annotation { "Feature Type Name" : "Feature", "Feature Type Description" : "" }
export const myFeature = defineFeature(function(context is Context, id is Id, definition is map)
    precondition{}
    {
        {
            var Q0;
            Q0=qCreatedBy(makeId("Front.planeOp"),FACE);
            var sketch = newSketch(context, id + "F0", { "sketchPlane" : qUnion([Q0])});
            skLineSegment(sketch, "E0", {"start": v(0, 0) * mm, "end": v(-59.66, 0) * mm, "construction": true});
            skArc(sketch, "E1", {"start": v(-4.94, 52) * mm, "mid": v(-30.96, 44.87) * mm, "end": v(-49.36, 25.14) * mm});
            skLineSegment(sketch, "E2", {"start": v(-4.94, 52) * mm, "end": v(-4.94, 48.83) * mm});
            skLineSegment(sketch, "E3", {"start": v(-4.94, 48.83) * mm, "end": v(2.13, 48.83) * mm});
            skLineSegment(sketch, "E4", {"start": v(2.13, 48.83) * mm, "end": v(4, 52) * mm});
            skLineSegment(sketch, "E5", {"start": v(4, 52) * mm, "end": v(31.08, 52) * mm});
            skLineSegment(sketch, "E6", {"start": v(31.08, 52) * mm, "end": v(32.87, 50.92) * mm});
            skLineSegment(sketch, "E7", {"start": v(32.87, 50.92) * mm, "end": v(38.57, 40.14) * mm});
            skLineSegment(sketch, "E8", {"start": v(38.57, 40.14) * mm, "end": v(45.19, 36.28) * mm});
            skLineSegment(sketch, "E9", {"start": v(45.19, 36.28) * mm, "end": v(45.19, 32) * mm});
            skLineSegment(sketch, "E10", {"start": v(45.19, 32) * mm, "end": v(39.54, 30.64) * mm});
            skLineSegment(sketch, "E11", {"start": v(39.54, 30.64) * mm, "end": v(37.92, 28.14) * mm});
            skLineSegment(sketch, "E12", {"start": v(37.92, 28.14) * mm, "end": v(2.13, 28.14) * mm});
            skLineSegment(sketch, "E13", {"start": v(2.13, 28.14) * mm, "end": v(2.13, 23.6) * mm});
            skLineSegment(sketch, "E14", {"start": v(2.13, 23.6) * mm, "end": v(17.62, 9.9) * mm});
            skLineSegment(sketch, "E15", {"start": v(17.62, 9.9) * mm, "end": v(45.2, 9.9) * mm});
            skLineSegment(sketch, "E16", {"start": v(45.2, 9.9) * mm, "end": v(45.2, 6.04) * mm});
            skLineSegment(sketch, "E17", {"start": v(45.2, 6.04) * mm, "end": v(57.9, 6.04) * mm});
            skLineSegment(sketch, "E18", {"start": v(57.9, 6.04) * mm, "end": v(59.26, 4.95) * mm});
            skLineSegment(sketch, "E19", {"start": v(59.26, 4.95) * mm, "end": v(59.26, 0) * mm});
            skLineSegment(sketch, "E20", {"start": v(-49.36, 25.14) * mm, "end": v(-53.32, 25.14) * mm});
            skLineSegment(sketch, "E21", {"start": v(-53.32, 25.14) * mm, "end": v(-53.32, 22.85) * mm});
            skLineSegment(sketch, "E22", {"start": v(-53.32, 22.85) * mm, "end": v(-56.28, 21.25) * mm});
            skLineSegment(sketch, "E23", {"start": v(-56.28, 21.25) * mm, "end": v(-56.28, 14.94) * mm});
            skLineSegment(sketch, "E24", {"start": v(-56.28, 14.94) * mm, "end": v(-57.5, 13.21) * mm});
            skLineSegment(sketch, "E25", {"start": v(-57.5, 13.21) * mm, "end": v(-58.56, 3.76) * mm});
            skLineSegment(sketch, "E26", {"start": v(-58.56, 3.76) * mm, "end": v(-58.56, 0) * mm});
            skLineSegment(sketch, "E27.MirrorCS", {"start": v(-56.28, -14.94) * mm, "end": v(-57.5, -13.21) * mm});
            skLineSegment(sketch, "E28.MirrorCS", {"start": v(-57.5, -13.21) * mm, "end": v(-58.56, -3.76) * mm});
            skLineSegment(sketch, "E29.MirrorCS", {"start": v(-58.56, -3.76) * mm, "end": v(-58.56, 0) * mm});
            skLineSegment(sketch, "E30.MirrorCS", {"start": v(-56.28, -21.25) * mm, "end": v(-56.28, -14.94) * mm});
            skLineSegment(sketch, "E31.MirrorCS", {"start": v(-53.32, -22.85) * mm, "end": v(-56.28, -21.25) * mm});
            skLineSegment(sketch, "E32.MirrorCS", {"start": v(-53.32, -25.14) * mm, "end": v(-53.32, -22.85) * mm});
            skLineSegment(sketch, "E33.MirrorCS", {"start": v(-49.36, -25.14) * mm, "end": v(-53.32, -25.14) * mm});
            skArc(sketch, "E34.MirrorCS", {"start": v(-4.94, -52) * mm, "mid": v(-30.96, -44.87) * mm, "end": v(-49.36, -25.14) * mm});
            skLineSegment(sketch, "E35.MirrorCS", {"start": v(-4.94, -52) * mm, "end": v(-4.94, -48.83) * mm});
            skLineSegment(sketch, "E36.MirrorCS", {"start": v(-4.94, -48.83) * mm, "end": v(2.13, -48.83) * mm});
            skLineSegment(sketch, "E37.MirrorCS", {"start": v(2.13, -48.83) * mm, "end": v(4, -52) * mm});
            skLineSegment(sketch, "E38.MirrorCS", {"start": v(4, -52) * mm, "end": v(31.08, -52) * mm});
            skLineSegment(sketch, "E39.MirrorCS", {"start": v(31.08, -52) * mm, "end": v(32.87, -50.92) * mm});
            skLineSegment(sketch, "E40.MirrorCS", {"start": v(38.57, -40.14) * mm, "end": v(45.19, -36.28) * mm});
            skLineSegment(sketch, "E41.MirrorCS", {"start": v(32.87, -50.92) * mm, "end": v(38.57, -40.14) * mm});
            skLineSegment(sketch, "E42", {"start": v(45.19, -36.28) * mm, "end": v(45.19, -31.9) * mm});
            skLineSegment(sketch, "E43", {"start": v(45.19, -31.9) * mm, "end": v(39.54, -30.54) * mm});
            skLineSegment(sketch, "E44", {"start": v(39.54, -30.54) * mm, "end": v(37.55, -27.38) * mm});
            skLineSegment(sketch, "E45", {"start": v(37.55, -27.38) * mm, "end": v(37.55, -12.3) * mm});
            skLineSegment(sketch, "E46", {"start": v(37.55, -12.3) * mm, "end": v(39.67, -9.9) * mm});
            skLineSegment(sketch, "E47", {"start": v(39.67, -9.9) * mm, "end": v(45.19, -9.9) * mm});
            skLineSegment(sketch, "E48", {"start": v(45.19, -9.9) * mm, "end": v(45.2, -6) * mm});
            skLineSegment(sketch, "E49", {"start": v(45.2, -6) * mm, "end": v(57.9, -6.04) * mm});
            skLineSegment(sketch, "E50", {"start": v(57.9, -6.04) * mm, "end": v(59.26, -4.79) * mm});
            skLineSegment(sketch, "E51", {"start": v(59.26, -4.79) * mm, "end": v(59.26, 0) * mm});
            skSolve(sketch);
        }
        {
            var Q0;
            Q0 = qSketchRegion(id + "F0", true);
            extrude(context, id + "F1", {"entities" : qUnion([Q0]), "depth" : 2 * mm, "offsetDistance" : 25 * mm});
        }
        {
            var Q0;
            Q0=makeQuery(id+"F1.opExtrude","SWEPT_BODY",BODY,{"disambiguationData":[OSD([sQuery(id+"F0.wireOp",EDGE,"E1"),sQuery(id+"F0.wireOp",EDGE,"E2"),sQuery(id+"F0.wireOp",EDGE,"E3"),sQuery(id+"F0.wireOp",EDGE,"E4"),sQuery(id+"F0.wireOp",EDGE,"E5"),sQuery(id+"F0.wireOp",EDGE,"E6"),sQuery(id+"F0.wireOp",EDGE,"E7"),sQuery(id+"F0.wireOp",EDGE,"E8"),sQuery(id+"F0.wireOp",EDGE,"E9"),sQuery(id+"F0.wireOp",EDGE,"E10"),sQuery(id+"F0.wireOp",EDGE,"E11"),sQuery(id+"F0.wireOp",EDGE,"E12"),sQuery(id+"F0.wireOp",EDGE,"E13"),sQuery(id+"F0.wireOp",EDGE,"E14"),sQuery(id+"F0.wireOp",EDGE,"E15"),sQuery(id+"F0.wireOp",EDGE,"E16"),sQuery(id+"F0.wireOp",EDGE,"E17"),sQuery(id+"F0.wireOp",EDGE,"E18"),sQuery(id+"F0.wireOp",EDGE,"E19"),sQuery(id+"F0.wireOp",EDGE,"E20"),sQuery(id+"F0.wireOp",EDGE,"E21"),sQuery(id+"F0.wireOp",EDGE,"E22"),sQuery(id+"F0.wireOp",EDGE,"E23"),sQuery(id+"F0.wireOp",EDGE,"E24"),sQuery(id+"F0.wireOp",EDGE,"E25"),sQuery(id+"F0.wireOp",EDGE,"E26"),sQuery(id+"F0.wireOp",EDGE,"E27.MirrorCS"),sQuery(id+"F0.wireOp",EDGE,"E28.MirrorCS"),sQuery(id+"F0.wireOp",EDGE,"E29.MirrorCS"),sQuery(id+"F0.wireOp",EDGE,"E30.MirrorCS"),sQuery(id+"F0.wireOp",EDGE,"E31.MirrorCS"),sQuery(id+"F0.wireOp",EDGE,"E32.MirrorCS"),sQuery(id+"F0.wireOp",EDGE,"E33.MirrorCS"),sQuery(id+"F0.wireOp",EDGE,"E34.MirrorCS"),sQuery(id+"F0.wireOp",EDGE,"E35.MirrorCS"),sQuery(id+"F0.wireOp",EDGE,"E36.MirrorCS"),sQuery(id+"F0.wireOp",EDGE,"E37.MirrorCS"),sQuery(id+"F0.wireOp",EDGE,"E38.MirrorCS"),sQuery(id+"F0.wireOp",EDGE,"E39.MirrorCS"),sQuery(id+"F0.wireOp",EDGE,"E40.MirrorCS"),sQuery(id+"F0.wireOp",EDGE,"E41.MirrorCS"),sQuery(id+"F0.wireOp",EDGE,"E42"),sQuery(id+"F0.wireOp",EDGE,"E43"),sQuery(id+"F0.wireOp",EDGE,"E44"),sQuery(id+"F0.wireOp",EDGE,"E45"),sQuery(id+"F0.wireOp",EDGE,"E46"),sQuery(id+"F0.wireOp",EDGE,"E47"),sQuery(id+"F0.wireOp",EDGE,"E48"),sQuery(id+"F0.wireOp",EDGE,"E49"),sQuery(id+"F0.wireOp",EDGE,"E50"),sQuery(id+"F0.wireOp",EDGE,"E51")])]});
            var Q1;
            Q1=makeQuery(id+"F1.opExtrude","CAP_VERTEX",VERTEX,{"disambiguationData":[OSD([sQuery(id+"F0.wireOp",EDGE,"E19"),sQuery(id+"F0.wireOp",EDGE,"E51")])],"isStart":false});
            transform(context, id + "F2", {"entities" : qUnion([Q0]), "transformType" : TransformType.SCALE_UNIFORMLY, "scale" : 1.25, "scalePoint" : qUnion([Q1]), "makeCopy" : false});
        }
        {
            var Q0;
            Q0=makeQuery(id+"F1.opExtrude","CAP_FACE",FACE,{"disambiguationData":[OSD([sQuery(id+"F0.wireOp",EDGE,"E1"),sQuery(id+"F0.wireOp",EDGE,"E2"),sQuery(id+"F0.wireOp",EDGE,"E3"),sQuery(id+"F0.wireOp",EDGE,"E4"),sQuery(id+"F0.wireOp",EDGE,"E5"),sQuery(id+"F0.wireOp",EDGE,"E6"),sQuery(id+"F0.wireOp",EDGE,"E7"),sQuery(id+"F0.wireOp",EDGE,"E8"),sQuery(id+"F0.wireOp",EDGE,"E9"),sQuery(id+"F0.wireOp",EDGE,"E10"),sQuery(id+"F0.wireOp",EDGE,"E11"),sQuery(id+"F0.wireOp",EDGE,"E12"),sQuery(id+"F0.wireOp",EDGE,"E13"),sQuery(id+"F0.wireOp",EDGE,"E14"),sQuery(id+"F0.wireOp",EDGE,"E15"),sQuery(id+"F0.wireOp",EDGE,"E16"),sQuery(id+"F0.wireOp",EDGE,"E17"),sQuery(id+"F0.wireOp",EDGE,"E18"),sQuery(id+"F0.wireOp",EDGE,"E19"),sQuery(id+"F0.wireOp",EDGE,"E20"),sQuery(id+"F0.wireOp",EDGE,"E21"),sQuery(id+"F0.wireOp",EDGE,"E22"),sQuery(id+"F0.wireOp",EDGE,"E23"),sQuery(id+"F0.wireOp",EDGE,"E24"),sQuery(id+"F0.wireOp",EDGE,"E25"),sQuery(id+"F0.wireOp",EDGE,"E26"),sQuery(id+"F0.wireOp",EDGE,"E27.MirrorCS"),sQuery(id+"F0.wireOp",EDGE,"E28.MirrorCS"),sQuery(id+"F0.wireOp",EDGE,"E29.MirrorCS"),sQuery(id+"F0.wireOp",EDGE,"E30.MirrorCS"),sQuery(id+"F0.wireOp",EDGE,"E31.MirrorCS"),sQuery(id+"F0.wireOp",EDGE,"E32.MirrorCS"),sQuery(id+"F0.wireOp",EDGE,"E33.MirrorCS"),sQuery(id+"F0.wireOp",EDGE,"E34.MirrorCS"),sQuery(id+"F0.wireOp",EDGE,"E35.MirrorCS"),sQuery(id+"F0.wireOp",EDGE,"E36.MirrorCS"),sQuery(id+"F0.wireOp",EDGE,"E37.MirrorCS"),sQuery(id+"F0.wireOp",EDGE,"E38.MirrorCS"),sQuery(id+"F0.wireOp",EDGE,"E39.MirrorCS"),sQuery(id+"F0.wireOp",EDGE,"E40.MirrorCS"),sQuery(id+"F0.wireOp",EDGE,"E41.MirrorCS"),sQuery(id+"F0.wireOp",EDGE,"E42"),sQuery(id+"F0.wireOp",EDGE,"E43"),sQuery(id+"F0.wireOp",EDGE,"E44"),sQuery(id+"F0.wireOp",EDGE,"E45"),sQuery(id+"F0.wireOp",EDGE,"E46"),sQuery(id+"F0.wireOp",EDGE,"E47"),sQuery(id+"F0.wireOp",EDGE,"E48"),sQuery(id+"F0.wireOp",EDGE,"E49"),sQuery(id+"F0.wireOp",EDGE,"E50"),sQuery(id+"F0.wireOp",EDGE,"E51")])],"isStart":false});
            var sketch = newSketch(context, id + "F3", { "sketchPlane" : qUnion([Q0])});
            skLineSegment(sketch, "E52.bottom", {"start": v(-24.37, -61.04) * mm, "end": v(-4.37, -61.04) * mm});
            skLineSegment(sketch, "E52.top", {"start": v(-24.37, -71.04) * mm, "end": v(-4.37, -71.04) * mm});
            skLineSegment(sketch, "E52.left", {"start": v(-24.37, -61.04) * mm, "end": v(-24.37, -71.04) * mm});
            skLineSegment(sketch, "E52.right", {"start": v(-4.37, -61.04) * mm, "end": v(-4.37, -71.04) * mm});
            skLineSegment(sketch, "E53", {"start": v(-88.01, 0) * mm, "end": v(59.26, 0) * mm, "construction": true});
            skLineSegment(sketch, "E54", {"start": v(-14.37, 0) * mm, "end": v(-14.37, -61.04) * mm, "construction": true});
            skLineSegment(sketch, "E55", {"start": v(-24.37, -71.04) * mm, "end": v(-62.79, -71.04) * mm});
            skLineSegment(sketch, "E56", {"start": v(-62.79, -71.04) * mm, "end": v(-72.79, -76.81) * mm});
            skLineSegment(sketch, "E57", {"start": v(-72.79, -76.81) * mm, "end": v(-72.79, -89.04) * mm});
            skLineSegment(sketch, "E58.MirrorCS", {"start": v(-4.37, -71.04) * mm, "end": v(34.04, -71.04) * mm});
            skLineSegment(sketch, "E59.MirrorCS", {"start": v(34.04, -71.04) * mm, "end": v(44.04, -76.81) * mm});
            skLineSegment(sketch, "E60.MirrorCS", {"start": v(44.04, -76.81) * mm, "end": v(44.04, -89.04) * mm});
            skLineSegment(sketch, "E61", {"start": v(-72.79, -89.04) * mm, "end": v(44.04, -89.04) * mm});
            skText(sketch, "E62", { "text": "EBON HAWK", "fontName": "OpenSans-Bold.ttf"});
            skLineSegment(sketch, "E63", {"start": v(-62.79, -89.04) * mm, "end": v(-42.58, -124.04) * mm});
            skLineSegment(sketch, "E64", {"start": v(-42.58, -124.04) * mm, "end": v(13.83, -124.04) * mm});
            skLineSegment(sketch, "E65", {"start": v(13.83, -124.04) * mm, "end": v(34.04, -89.04) * mm});
            skLineSegment(sketch, "E66.0", {"start": v(8.06, -114.04) * mm, "end": v(22.5, -89.04) * mm});
            skLineSegment(sketch, "E66.1", {"start": v(-36.8, -114.04) * mm, "end": v(8.06, -114.04) * mm});
            skLineSegment(sketch, "E66.2", {"start": v(-51.24, -89.04) * mm, "end": v(-36.8, -114.04) * mm});
            const initialGuessF3  = {"E62": [-0.05779, -0.08504, 1, 0, 0.01]};
            skSetInitialGuess(sketch, initialGuessF3);
            skSolve(sketch);
        }
        {
            var Q0;
            Q0 = qSketchRegion(id + "F3", true);
            var Q1;
            Q1=makeQuery(id+"F1.opExtrude","CAP_FACE",FACE,{"disambiguationData":[OSD([sQuery(id+"F0.wireOp",EDGE,"E1"),sQuery(id+"F0.wireOp",EDGE,"E2"),sQuery(id+"F0.wireOp",EDGE,"E3"),sQuery(id+"F0.wireOp",EDGE,"E4"),sQuery(id+"F0.wireOp",EDGE,"E5"),sQuery(id+"F0.wireOp",EDGE,"E6"),sQuery(id+"F0.wireOp",EDGE,"E7"),sQuery(id+"F0.wireOp",EDGE,"E8"),sQuery(id+"F0.wireOp",EDGE,"E9"),sQuery(id+"F0.wireOp",EDGE,"E10"),sQuery(id+"F0.wireOp",EDGE,"E11"),sQuery(id+"F0.wireOp",EDGE,"E12"),sQuery(id+"F0.wireOp",EDGE,"E13"),sQuery(id+"F0.wireOp",EDGE,"E14"),sQuery(id+"F0.wireOp",EDGE,"E15"),sQuery(id+"F0.wireOp",EDGE,"E16"),sQuery(id+"F0.wireOp",EDGE,"E17"),sQuery(id+"F0.wireOp",EDGE,"E18"),sQuery(id+"F0.wireOp",EDGE,"E19"),sQuery(id+"F0.wireOp",EDGE,"E20"),sQuery(id+"F0.wireOp",EDGE,"E21"),sQuery(id+"F0.wireOp",EDGE,"E22"),sQuery(id+"F0.wireOp",EDGE,"E23"),sQuery(id+"F0.wireOp",EDGE,"E24"),sQuery(id+"F0.wireOp",EDGE,"E25"),sQuery(id+"F0.wireOp",EDGE,"E26"),sQuery(id+"F0.wireOp",EDGE,"E27.MirrorCS"),sQuery(id+"F0.wireOp",EDGE,"E28.MirrorCS"),sQuery(id+"F0.wireOp",EDGE,"E29.MirrorCS"),sQuery(id+"F0.wireOp",EDGE,"E30.MirrorCS"),sQuery(id+"F0.wireOp",EDGE,"E31.MirrorCS"),sQuery(id+"F0.wireOp",EDGE,"E32.MirrorCS"),sQuery(id+"F0.wireOp",EDGE,"E33.MirrorCS"),sQuery(id+"F0.wireOp",EDGE,"E34.MirrorCS"),sQuery(id+"F0.wireOp",EDGE,"E35.MirrorCS"),sQuery(id+"F0.wireOp",EDGE,"E36.MirrorCS"),sQuery(id+"F0.wireOp",EDGE,"E37.MirrorCS"),sQuery(id+"F0.wireOp",EDGE,"E38.MirrorCS"),sQuery(id+"F0.wireOp",EDGE,"E39.MirrorCS"),sQuery(id+"F0.wireOp",EDGE,"E40.MirrorCS"),sQuery(id+"F0.wireOp",EDGE,"E41.MirrorCS"),sQuery(id+"F0.wireOp",EDGE,"E42"),sQuery(id+"F0.wireOp",EDGE,"E43"),sQuery(id+"F0.wireOp",EDGE,"E44"),sQuery(id+"F0.wireOp",EDGE,"E45"),sQuery(id+"F0.wireOp",EDGE,"E46"),sQuery(id+"F0.wireOp",EDGE,"E47"),sQuery(id+"F0.wireOp",EDGE,"E48"),sQuery(id+"F0.wireOp",EDGE,"E49"),sQuery(id+"F0.wireOp",EDGE,"E50"),sQuery(id+"F0.wireOp",EDGE,"E51")])],"isStart":true});
            extrude(context, id + "F4", {"entities" : qUnion([Q0]), "operationType" : NewBodyOperationType.ADD, "endBound" : BoundingType.UP_TO_SURFACE, "oppositeDirection" : true, "depth" : 25 * mm, "endBoundEntityFace" : qUnion([Q1]), "offsetDistance" : 25 * mm});
        }
        {
            var Q0;
            Q0=makeQuery(id+"F3.imprint","IMPRINT",FACE,{"disambiguationData":[TD([[makeQuery(id+"F3.imprint","IMPRINT",EDGE,{"derivedFrom":sQuery(id+"F3.wireOp",EDGE,"E62.sketch_text.stroke-24")}),1.0]])]});
            var Q1;
            Q1=makeQuery(id+"F3.imprint","IMPRINT",FACE,{"disambiguationData":[TD([[makeQuery(id+"F3.imprint","IMPRINT",EDGE,{"derivedFrom":sQuery(id+"F3.wireOp",EDGE,"E62.sketch_text.stroke-31")}),1.0]])]});
            var Q2;
            Q2=makeQuery(id+"F3.imprint","IMPRINT",FACE,{"disambiguationData":[TD([[makeQuery(id+"F3.imprint","IMPRINT",EDGE,{"derivedFrom":sQuery(id+"F3.wireOp",EDGE,"E62.sketch_text.stroke-45")}),1.0]])]});
            var Q3;
            Q3=makeQuery(id+"F3.imprint","IMPRINT",FACE,{"disambiguationData":[TD([[makeQuery(id+"F3.imprint","IMPRINT",EDGE,{"derivedFrom":sQuery(id+"F3.wireOp",EDGE,"E62.sketch_text.stroke-85")}),1.0]])]});
            var Q4;
            {var subQ0=sQuery(id+"F0.wireOp",EDGE,"E51");var subQ1=sQuery(id+"F0.wireOp",EDGE,"E50");var subQ2=sQuery(id+"F0.wireOp",EDGE,"E49");var subQ3=sQuery(id+"F0.wireOp",EDGE,"E48");var subQ4=sQuery(id+"F0.wireOp",EDGE,"E47");var subQ5=sQuery(id+"F0.wireOp",EDGE,"E46");var subQ6=sQuery(id+"F0.wireOp",EDGE,"E45");var subQ7=sQuery(id+"F0.wireOp",EDGE,"E44");var subQ8=sQuery(id+"F0.wireOp",EDGE,"E43");var subQ9=sQuery(id+"F0.wireOp",EDGE,"E42");var subQ10=sQuery(id+"F0.wireOp",EDGE,"E41.MirrorCS");var subQ11=sQuery(id+"F0.wireOp",EDGE,"E40.MirrorCS");var subQ12=sQuery(id+"F0.wireOp",EDGE,"E39.MirrorCS");var subQ13=sQuery(id+"F0.wireOp",EDGE,"E38.MirrorCS");var subQ14=sQuery(id+"F0.wireOp",EDGE,"E37.MirrorCS");var subQ15=sQuery(id+"F0.wireOp",EDGE,"E36.MirrorCS");var subQ16=sQuery(id+"F0.wireOp",EDGE,"E35.MirrorCS");var subQ17=sQuery(id+"F0.wireOp",EDGE,"E34.MirrorCS");var subQ18=sQuery(id+"F0.wireOp",EDGE,"E33.MirrorCS");var subQ19=sQuery(id+"F0.wireOp",EDGE,"E32.MirrorCS");var subQ20=sQuery(id+"F0.wireOp",EDGE,"E31.MirrorCS");var subQ21=sQuery(id+"F0.wireOp",EDGE,"E30.MirrorCS");var subQ22=sQuery(id+"F0.wireOp",EDGE,"E29.MirrorCS");var subQ23=sQuery(id+"F0.wireOp",EDGE,"E28.MirrorCS");var subQ24=sQuery(id+"F0.wireOp",EDGE,"E27.MirrorCS");var subQ25=sQuery(id+"F0.wireOp",EDGE,"E26");var subQ26=sQuery(id+"F0.wireOp",EDGE,"E25");var subQ27=sQuery(id+"F0.wireOp",EDGE,"E24");var subQ28=sQuery(id+"F0.wireOp",EDGE,"E23");var subQ29=sQuery(id+"F0.wireOp",EDGE,"E22");var subQ30=sQuery(id+"F0.wireOp",EDGE,"E21");var subQ31=sQuery(id+"F0.wireOp",EDGE,"E20");var subQ32=sQuery(id+"F0.wireOp",EDGE,"E19");var subQ33=sQuery(id+"F0.wireOp",EDGE,"E18");var subQ34=sQuery(id+"F0.wireOp",EDGE,"E17");var subQ35=sQuery(id+"F0.wireOp",EDGE,"E16");var subQ36=sQuery(id+"F0.wireOp",EDGE,"E15");var subQ37=sQuery(id+"F0.wireOp",EDGE,"E14");var subQ38=sQuery(id+"F0.wireOp",EDGE,"E13");var subQ39=sQuery(id+"F0.wireOp",EDGE,"E12");var subQ40=sQuery(id+"F0.wireOp",EDGE,"E11");var subQ41=sQuery(id+"F0.wireOp",EDGE,"E10");var subQ42=sQuery(id+"F0.wireOp",EDGE,"E9");var subQ43=sQuery(id+"F0.wireOp",EDGE,"E8");var subQ44=sQuery(id+"F0.wireOp",EDGE,"E7");var subQ45=sQuery(id+"F0.wireOp",EDGE,"E6");var subQ46=sQuery(id+"F0.wireOp",EDGE,"E5");var subQ47=sQuery(id+"F0.wireOp",EDGE,"E4");var subQ48=sQuery(id+"F0.wireOp",EDGE,"E3");var subQ49=sQuery(id+"F0.wireOp",EDGE,"E2");var subQ50=sQuery(id+"F0.wireOp",EDGE,"E1");Q4=makeQuery(id+"F4.boolean.opBoolean","MERGE",FACE,{"derivedFrom":[makeQuery(id+"F1.opExtrude","CAP_FACE",FACE,{"disambiguationData":[OSD([subQ50,subQ49,subQ48,subQ47,subQ46,subQ45,subQ44,subQ43,subQ42,subQ41,subQ40,subQ39,subQ38,subQ37,subQ36,subQ35,subQ34,subQ33,subQ32,subQ31,subQ30,subQ29,subQ28,subQ27,subQ26,subQ25,subQ24,subQ23,subQ22,subQ21,subQ20,subQ19,subQ18,subQ17,subQ16,subQ15,subQ14,subQ13,subQ12,subQ11,subQ10,subQ9,subQ8,subQ7,subQ6,subQ5,subQ4,subQ3,subQ2,subQ1,subQ0])],"isStart":true}),makeQuery(id+"F4.opExtrude","CAP_FACE",FACE,{"disambiguationData":[OSD([subQ50,subQ49,subQ48,subQ47,subQ46,subQ45,subQ44,subQ43,subQ42,subQ41,subQ40,subQ39,subQ38,subQ37,subQ36,subQ35,subQ34,subQ33,subQ32,subQ31,subQ30,subQ29,subQ28,subQ27,subQ26,subQ25,subQ24,subQ23,subQ22,subQ21,subQ20,subQ19,subQ18,subQ17,subQ16,subQ15,subQ14,subQ13,subQ12,subQ11,subQ10,subQ9,subQ8,subQ7,subQ6,subQ5,subQ4,subQ3,subQ2,subQ1,subQ0])],"isStart":false})]});}
            extrude(context, id + "F5", {"entities" : qUnion([Q0, Q1, Q2, Q3]), "endBound" : BoundingType.UP_TO_SURFACE, "oppositeDirection" : true, "depth" : 25 * mm, "endBoundEntityFace" : qUnion([Q4]), "offsetDistance" : 25 * mm});
        }
        {
            var Q0;
            Q0=makeQuery(id+"F3.imprint","IMPRINT",FACE,{"disambiguationData":[TD([[makeQuery(id+"F3.imprint","IMPRINT",EDGE,{"derivedFrom":sQuery(id+"F3.wireOp",EDGE,"E52.top")}),-1.0]])]});
            var sketch = newSketch(context, id + "F6", { "sketchPlane" : qUnion([Q0])});
            skLineSegment(sketch, "E67.bottom", {"start": v(-46.66, -75.12) * mm, "end": v(-45.36, -75.12) * mm});
            skLineSegment(sketch, "E67.top", {"start": v(-46.66, -85.04) * mm, "end": v(-45.36, -85.04) * mm});
            skLineSegment(sketch, "E67.left", {"start": v(-46.66, -75.12) * mm, "end": v(-46.66, -85.04) * mm});
            skLineSegment(sketch, "E67.right", {"start": v(-45.36, -75.12) * mm, "end": v(-45.36, -85.04) * mm});
            skLineSegment(sketch, "E68.bottom", {"start": v(-35.79, -74.97) * mm, "end": v(-34.49, -74.97) * mm});
            skLineSegment(sketch, "E68.top", {"start": v(-35.79, -85.18) * mm, "end": v(-34.49, -85.18) * mm});
            skLineSegment(sketch, "E68.left", {"start": v(-35.79, -74.97) * mm, "end": v(-35.79, -85.18) * mm});
            skLineSegment(sketch, "E68.right", {"start": v(-34.49, -74.97) * mm, "end": v(-34.49, -85.18) * mm});
            skLineSegment(sketch, "E69.bottom", {"start": v(0.04, -75.08) * mm, "end": v(1.34, -75.08) * mm});
            skLineSegment(sketch, "E69.top", {"start": v(0.04, -82.68) * mm, "end": v(1.34, -82.68) * mm});
            skLineSegment(sketch, "E69.left", {"start": v(0.04, -75.08) * mm, "end": v(0.04, -82.68) * mm});
            skLineSegment(sketch, "E69.right", {"start": v(1.34, -75.08) * mm, "end": v(1.34, -82.68) * mm});
            skSolve(sketch);
        }
        {
            var Q0;
            Q0 = qSketchRegion(id + "F6", true);
            var Q1;
            {var subQ0=sQuery(id+"F0.wireOp",EDGE,"E51");var subQ1=sQuery(id+"F0.wireOp",EDGE,"E50");var subQ2=sQuery(id+"F0.wireOp",EDGE,"E49");var subQ3=sQuery(id+"F0.wireOp",EDGE,"E48");var subQ4=sQuery(id+"F0.wireOp",EDGE,"E47");var subQ5=sQuery(id+"F0.wireOp",EDGE,"E46");var subQ6=sQuery(id+"F0.wireOp",EDGE,"E45");var subQ7=sQuery(id+"F0.wireOp",EDGE,"E44");var subQ8=sQuery(id+"F0.wireOp",EDGE,"E43");var subQ9=sQuery(id+"F0.wireOp",EDGE,"E42");var subQ10=sQuery(id+"F0.wireOp",EDGE,"E41.MirrorCS");var subQ11=sQuery(id+"F0.wireOp",EDGE,"E40.MirrorCS");var subQ12=sQuery(id+"F0.wireOp",EDGE,"E39.MirrorCS");var subQ13=sQuery(id+"F0.wireOp",EDGE,"E38.MirrorCS");var subQ14=sQuery(id+"F0.wireOp",EDGE,"E37.MirrorCS");var subQ15=sQuery(id+"F0.wireOp",EDGE,"E36.MirrorCS");var subQ16=sQuery(id+"F0.wireOp",EDGE,"E35.MirrorCS");var subQ17=sQuery(id+"F0.wireOp",EDGE,"E34.MirrorCS");var subQ18=sQuery(id+"F0.wireOp",EDGE,"E33.MirrorCS");var subQ19=sQuery(id+"F0.wireOp",EDGE,"E32.MirrorCS");var subQ20=sQuery(id+"F0.wireOp",EDGE,"E31.MirrorCS");var subQ21=sQuery(id+"F0.wireOp",EDGE,"E30.MirrorCS");var subQ22=sQuery(id+"F0.wireOp",EDGE,"E29.MirrorCS");var subQ23=sQuery(id+"F0.wireOp",EDGE,"E28.MirrorCS");var subQ24=sQuery(id+"F0.wireOp",EDGE,"E27.MirrorCS");var subQ25=sQuery(id+"F0.wireOp",EDGE,"E26");var subQ26=sQuery(id+"F0.wireOp",EDGE,"E25");var subQ27=sQuery(id+"F0.wireOp",EDGE,"E24");var subQ28=sQuery(id+"F0.wireOp",EDGE,"E23");var subQ29=sQuery(id+"F0.wireOp",EDGE,"E22");var subQ30=sQuery(id+"F0.wireOp",EDGE,"E21");var subQ31=sQuery(id+"F0.wireOp",EDGE,"E20");var subQ32=sQuery(id+"F0.wireOp",EDGE,"E19");var subQ33=sQuery(id+"F0.wireOp",EDGE,"E18");var subQ34=sQuery(id+"F0.wireOp",EDGE,"E17");var subQ35=sQuery(id+"F0.wireOp",EDGE,"E16");var subQ36=sQuery(id+"F0.wireOp",EDGE,"E15");var subQ37=sQuery(id+"F0.wireOp",EDGE,"E14");var subQ38=sQuery(id+"F0.wireOp",EDGE,"E13");var subQ39=sQuery(id+"F0.wireOp",EDGE,"E12");var subQ40=sQuery(id+"F0.wireOp",EDGE,"E11");var subQ41=sQuery(id+"F0.wireOp",EDGE,"E10");var subQ42=sQuery(id+"F0.wireOp",EDGE,"E9");var subQ43=sQuery(id+"F0.wireOp",EDGE,"E8");var subQ44=sQuery(id+"F0.wireOp",EDGE,"E7");var subQ45=sQuery(id+"F0.wireOp",EDGE,"E6");var subQ46=sQuery(id+"F0.wireOp",EDGE,"E5");var subQ47=sQuery(id+"F0.wireOp",EDGE,"E4");var subQ48=sQuery(id+"F0.wireOp",EDGE,"E3");var subQ49=sQuery(id+"F0.wireOp",EDGE,"E2");var subQ50=sQuery(id+"F0.wireOp",EDGE,"E1");Q1=makeQuery(id+"F4.boolean.opBoolean","MERGE",FACE,{"derivedFrom":[makeQuery(id+"F1.opExtrude","CAP_FACE",FACE,{"disambiguationData":[OSD([subQ50,subQ49,subQ48,subQ47,subQ46,subQ45,subQ44,subQ43,subQ42,subQ41,subQ40,subQ39,subQ38,subQ37,subQ36,subQ35,subQ34,subQ33,subQ32,subQ31,subQ30,subQ29,subQ28,subQ27,subQ26,subQ25,subQ24,subQ23,subQ22,subQ21,subQ20,subQ19,subQ18,subQ17,subQ16,subQ15,subQ14,subQ13,subQ12,subQ11,subQ10,subQ9,subQ8,subQ7,subQ6,subQ5,subQ4,subQ3,subQ2,subQ1,subQ0])],"isStart":true}),makeQuery(id+"F4.opExtrude","CAP_FACE",FACE,{"disambiguationData":[OSD([subQ50,subQ49,subQ48,subQ47,subQ46,subQ45,subQ44,subQ43,subQ42,subQ41,subQ40,subQ39,subQ38,subQ37,subQ36,subQ35,subQ34,subQ33,subQ32,subQ31,subQ30,subQ29,subQ28,subQ27,subQ26,subQ25,subQ24,subQ23,subQ22,subQ21,subQ20,subQ19,subQ18,subQ17,subQ16,subQ15,subQ14,subQ13,subQ12,subQ11,subQ10,subQ9,subQ8,subQ7,subQ6,subQ5,subQ4,subQ3,subQ2,subQ1,subQ0])],"isStart":false})]});}
            extrude(context, id + "F7", {"entities" : qUnion([Q0]), "operationType" : NewBodyOperationType.ADD, "endBound" : BoundingType.UP_TO_SURFACE, "oppositeDirection" : true, "depth" : 25 * mm, "endBoundEntityFace" : qUnion([Q1]), "offsetDistance" : 25 * mm});
        }
        {
            var Q0;
            Q0=makeQuery(id+"F4.opExtrude","SWEPT_EDGE",EDGE,{"disambiguationData":[OSD([sQuery(id+"F3.wireOp",EDGE,"E55"),sQuery(id+"F3.wireOp",EDGE,"E56")])]});
            var Q1;
            Q1=makeQuery(id+"F4.opExtrude","SWEPT_EDGE",EDGE,{"disambiguationData":[OSD([sQuery(id+"F3.wireOp",EDGE,"E56"),sQuery(id+"F3.wireOp",EDGE,"E57")])]});
            var Q2;
            Q2=makeQuery(id+"F4.opExtrude","SWEPT_EDGE",EDGE,{"disambiguationData":[OSD([sQuery(id+"F3.wireOp",EDGE,"E57"),sQuery(id+"F3.wireOp",EDGE,"E61")])]});
            var Q3;
            Q3=makeQuery(id+"F4.opExtrude","SWEPT_EDGE",EDGE,{"disambiguationData":[OSD([sQuery(id+"F3.wireOp",EDGE,"E58.MirrorCS"),sQuery(id+"F3.wireOp",EDGE,"E59.MirrorCS")])]});
            var Q4;
            Q4=makeQuery(id+"F4.opExtrude","SWEPT_EDGE",EDGE,{"disambiguationData":[OSD([sQuery(id+"F3.wireOp",EDGE,"E59.MirrorCS"),sQuery(id+"F3.wireOp",EDGE,"E60.MirrorCS")])]});
            var Q5;
            Q5=makeQuery(id+"F4.opExtrude","SWEPT_EDGE",EDGE,{"disambiguationData":[OSD([sQuery(id+"F3.wireOp",EDGE,"E60.MirrorCS"),sQuery(id+"F3.wireOp",EDGE,"E61")])]});
            var Q6;
            Q6=makeQuery(id+"F4.opExtrude","SWEPT_EDGE",EDGE,{"disambiguationData":[OSD([sQuery(id+"F3.wireOp",EDGE,"E66.1"),sQuery(id+"F3.wireOp",EDGE,"E66.2")])]});
            var Q7;
            Q7=makeQuery(id+"F4.opExtrude","SWEPT_EDGE",EDGE,{"disambiguationData":[OSD([sQuery(id+"F3.wireOp",EDGE,"E66.0"),sQuery(id+"F3.wireOp",EDGE,"E66.1")])]});
            fillet(context, id + "F8", {"entities" : qUnion([Q0, Q1, Q2, Q3, Q4, Q5, Q6, Q7]), "radius" : 5 * mm, "tangentPropagation" : true, "allowEdgeOverflow" : false});
        }
        {
            var Q0;
            Q0=makeQuery(id+"F4.opExtrude","SWEPT_EDGE",EDGE,{"disambiguationData":[OSD([sQuery(id+"F3.wireOp",EDGE,"E63"),sQuery(id+"F3.wireOp",EDGE,"E64")])]});
            var Q1;
            Q1=makeQuery(id+"F4.opExtrude","SWEPT_EDGE",EDGE,{"disambiguationData":[OSD([sQuery(id+"F3.wireOp",EDGE,"E64"),sQuery(id+"F3.wireOp",EDGE,"E65")])]});
            fillet(context, id + "F9", {"entities" : qUnion([Q0, Q1]), "radius" : 15 * mm, "tangentPropagation" : true, "allowEdgeOverflow" : false});
        }
        {
            var Q0;
            Q0=qCreatedBy(makeId("Right.planeOp"),FACE);
            var sketch = newSketch(context, id + "F10", { "sketchPlane" : qUnion([Q0])});
            skLineSegment(sketch, "E70.bottom", {"start": v(-2, 67.01) * mm, "end": v(-1.5, 67.01) * mm});
            skLineSegment(sketch, "E70.top", {"start": v(-2, -124.04) * mm, "end": v(-1.5, -124.04) * mm});
            skLineSegment(sketch, "E70.left", {"start": v(-2, 67.01) * mm, "end": v(-2, -124.04) * mm});
            skLineSegment(sketch, "E70.right", {"start": v(-1.5, 67.01) * mm, "end": v(-1.5, -124.04) * mm});
            skSolve(sketch);
        }
        {
            var Q0;
            Q0 = qSketchRegion(id + "F10", true);
            extrude(context, id + "F11", {"entities" : qUnion([Q0]), "operationType" : NewBodyOperationType.REMOVE, "endBound" : BoundingType.THROUGH_ALL, "oppositeDirection" : true, "depth" : 25 * mm, "offsetDistance" : 25 * mm, "hasSecondDirection" : true, "secondDirectionBound" : SecondDirectionBoundingType.THROUGH_ALL, "secondDirectionOppositeDirection" : false, "secondDirectionDepth" : 25 * mm});
        }
    });